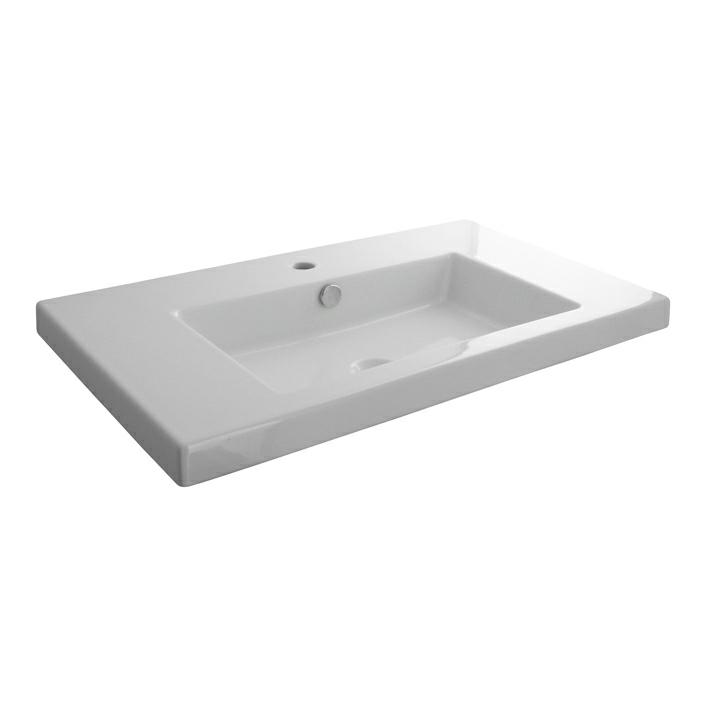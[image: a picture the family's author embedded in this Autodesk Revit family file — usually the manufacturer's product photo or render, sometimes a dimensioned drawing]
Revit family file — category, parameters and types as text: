
# Revit family: PGR_Noken_WlHngWshBsns_Square-80
name_source: partatom
category: Plumbing Fixtures
revit_build: Autodesk Revit 2017 (Build: 20171027_0315(x64)
units: mm (PartAtom-declared; Revit-internal decimal feet)

## family parameters
Always vertical = Yes
Cut with Voids When Loaded = No
Host = Wall
OmniClass Number = 23.45.05.14.14
OmniClass Title = Sinks/Lavatories
Part Type = Normal
Room Calculation Point = No
Round Connector Dimension = Use Diameter
Shared = Yes

## types (2) — shared parameters
AccessibilityPerformance = See ProductInformation for technical PDF
AssetType = Fixed
Category = Pr_40_20_96_96: Wall hung wash basins
CodePerformance = EN 14688 , EN 31
Collection = Square
Color = White
DiameterCW = 20 mm
DiameterHW = 20 mm
DrainSize = 46 mm
DurationUnit = Year
Features = See ProductInformation for technical PDF
Finish = White
FlowPressure = 0.0
FlowRate = CL-10
Height = 850 mm  [stored 2.78871 ft]
IfcExportAs = IfcSanitaryTerminalType
IfcExportType = WashHandBasin
ManufacturerURL = www.noken.com
Material = Fireclay
MaterialCeramic = PGR_Noken_Porcelain_White
MaterialMetal = PGR_Noken_Brass_Chrome
NBSDescription = Wall hung wash basins
NBSReference = 45-35-70/369
NettWeight = 20.3
NominalDepth = 90 mm  [stored 0.295276 ft]
NominalHeight = 90 mm  [stored 0.295276 ft]
NominalLength = 450 mm  [stored 1.47638 ft]
NominalWidth = 800 mm
Overflow = Yes
ProductInformation = http://calidad.info-grupo.com:8081
Reference = -
Size = 450x800x90mm
Status = UNSET
SustainabilityPerformance = See ProductInformation for technical PDF
TapHoles = 1
TechnicalDrawing = See ProductInformation for technical PDF
URL = www.noken.com
Uniclass2015Code = Pr_40_20_96_96
Uniclass2015Title = Wall-hung wash basins
Uniclass2015Version = V1_9
Version = 1
WarrantyDescription = See ProductInformation for technical PDF
WarrantyDurationUnit = Year
WashHandBasinMounting = WallHung
WashHandBasinType = HandRinse
WaterInlet = 1/2"
zero-valued in all types: CWFU, HWFU, MountingOffset, WFU

## per-type parameters (varying)
| type | BIMObjectName | ConnectorDistance1 | ConnectorDistance2 | Description | Model | ModelNumber | ModelReference | Name | Vs1 | Vs2 |
| Center-100090018 | PGR_Noken_WallHungWashBasins_Square_White-800x450x90mm-100090018 | 400 mm  [stored 1.31234 ft] | 125 mm  [stored 0.410105 ft] | Square 80 cm wall hung basin with centered bowl, overflow and fixing kit. Made in Fireclay. Complies with the standards EN 14688 and EN 31 . 10 years warranty for the ceramic and 2 for the non-ceramic components. | 100090018 | 100090018 | LAV. CITY 80CM SENO CENT. BLANCO | WallHungWashBasins_Square_White-800x450x90mm-100090018 | Yes | No |
| Right-100090019 | PGR_Noken_WallHungWashBasins_Square_White-800x450x90mm-100090019 | 299 mm  [stored 0.980971 ft] | 120 mm  [stored 0.393701 ft] | Square 80 cm wall hung basin with right offset bowl, overflow and fixing kit. Made in Fireclay. Complies with the standards EN 14688 and EN 31 . 10 years warranty for the ceramic and 2 for the non-ceramic components. | 100090019 | 100090019 | LAV. CITY 80CM SENO DER. BLANCO | WallHungWashBasins_Square_White-800x450x90mm-100090019 | No | Yes |

note: source unit labels omitted for FlowPressure — the stored unit's dimension contradicts the parameter name (converter mislabeling)

note: [stored X ft] marks values corroborated as IEEE doubles in the binary element streams (Revit-internal decimal feet)

## geometry (parser evidence)
native form markers: Blend x4, Sweep x12
no freeform markers — native parametric forms only
